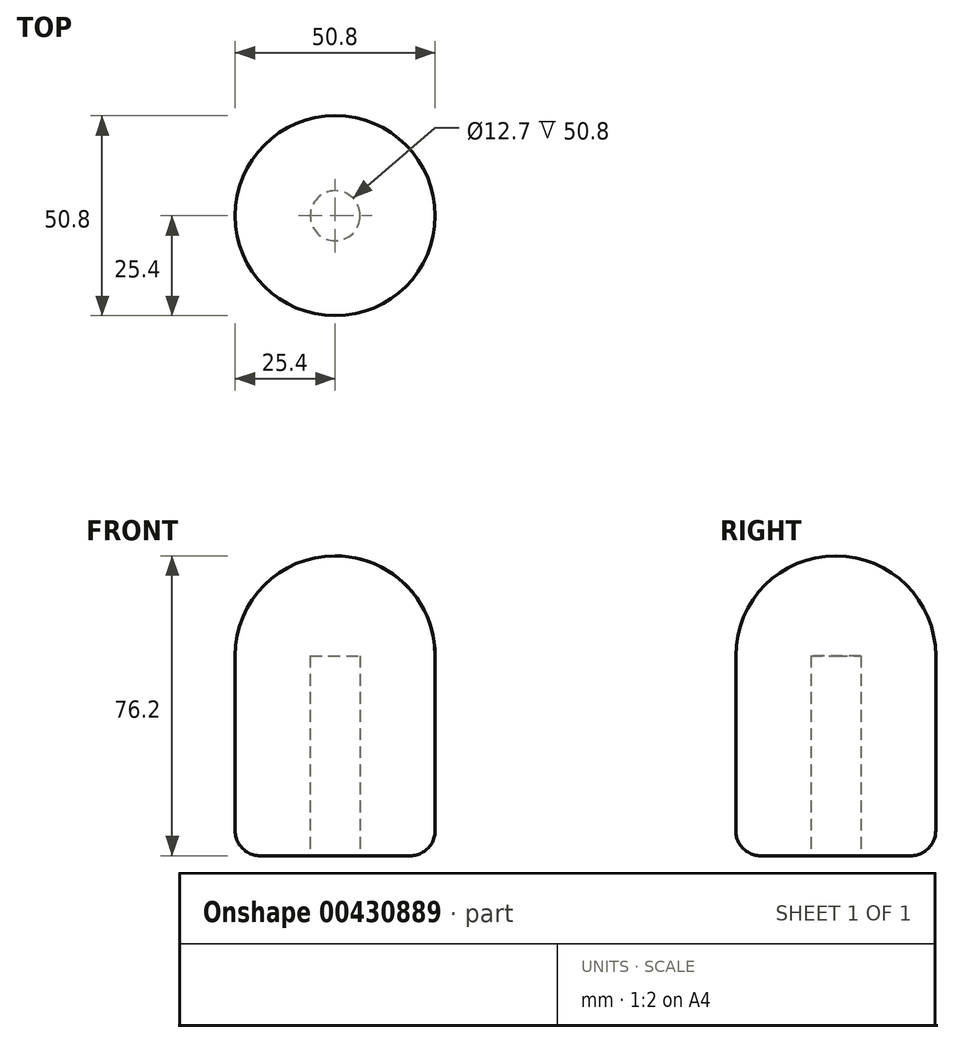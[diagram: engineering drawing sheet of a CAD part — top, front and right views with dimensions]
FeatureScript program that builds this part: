
annotation { "Feature Type Name" : "Feature", "Feature Type Description" : "" }
export const myFeature = defineFeature(function(context is Context, id is Id, definition is map)
    precondition{}
    {
        {
            var Q0;
            Q0=qCreatedBy(makeId("Front.planeOp"),FACE);
            var sketch = newSketch(context, id + "F0", { "sketchPlane" : qUnion([Q0])});
            skArc(sketch, "E0", {"start": v(0, 25.4) * mm, "mid": v(-25.4, 0) * mm, "end": v(0, -25.4) * mm});
            skLineSegment(sketch, "E1.bottom", {"start": v(-25.4, 0) * mm, "end": v(0, 0) * mm});
            skLineSegment(sketch, "E1.top", {"start": v(-19.05, -50.8) * mm, "end": v(0, -50.8) * mm});
            skLineSegment(sketch, "E1.left", {"start": v(-25.4, 0) * mm, "end": v(-25.4, -44.45) * mm});
            skPoint(sketch, "E2.visualSharp", {"position": v(-25.4, -50.8) * mm});
            skArc(sketch, "E2.filletArc", {"start": v(-25.4, -44.45) * mm, "mid": v(-23.54, -48.94) * mm, "end": v(-19.05, -50.8) * mm});
            skPoint(sketch, "E3.visualSharp", {"position": v(25.35, -50.8) * mm});
            skPoint(sketch, "E4", {"position": v(0, -50.8) * mm});
            skLineSegment(sketch, "E5", {"start": v(0, 25.4) * mm, "end": v(0, -50.8) * mm});
            skPoint(sketch, "E1.right.start.orphan", {"position": v(25.35, 0) * mm});
            skSolve(sketch);
        }
        {
            var Q0;
            {var subQ3=sQuery(id+"F0.wireOp",EDGE,"E1.bottom");Q0=makeQuery(id+"F0.imprint","IMPRINT",FACE,{"disambiguationData":[TD([[makeQuery(id+"F0.imprint","IMPRINT",EDGE,{"derivedFrom":subQ3}),1.0]])]});}
            var Q1;
            {var subQ3=sQuery(id+"F0.wireOp",EDGE,"E1.bottom");Q1=makeQuery(id+"F0.imprint","IMPRINT",FACE,{"disambiguationData":[TD([[makeQuery(id+"F0.imprint","IMPRINT",EDGE,{"derivedFrom":subQ3}),-1.0]])]});}
            var Q2;
            {var subQ1=sQuery(id+"F0.wireOp",EDGE,"E1.top");Q2=makeQuery(id+"F0.imprint","IMPRINT",FACE,{"disambiguationData":[TD([[makeQuery(id+"F0.imprint","IMPRINT",EDGE,{"derivedFrom":subQ1}),1.0]])]});}
            var Q3;
            Q3=sQuery(id+"F0.wireOp",EDGE,"E5");
            revolve(context, id + "F1", {"entities" : qUnion([Q0, Q1, Q2]), "axis" : qUnion([Q3]), "revolveType" : RevolveType.FULL});
        }
        {
            var Q0;
            Q0=makeQuery(id+"F1.opRevolve","SWEPT_FACE",FACE,{"disambiguationData":[OSD([sQuery(id+"F0.wireOp",EDGE,"E1.top")])]});
            var sketch = newSketch(context, id + "F2", { "sketchPlane" : qUnion([Q0])});
            skCircle(sketch, "E6", {"center": v(0, 0) * mm, "radius": 6.35 * mm});
            skSolve(sketch);
        }
        {
            var Q0;
            Q0=makeQuery(id+"F2.imprint","IMPRINT",FACE,{"disambiguationData":[TD([[makeQuery(id+"F2.imprint","IMPRINT",EDGE,{"derivedFrom":sQuery(id+"F2.wireOp",EDGE,"E6")}),1.0]])]});
            extrude(context, id + "F3", {"entities" : qUnion([Q0]), "operationType" : NewBodyOperationType.REMOVE, "oppositeDirection" : true, "depth" : 50.8 * mm});
        }
    });
